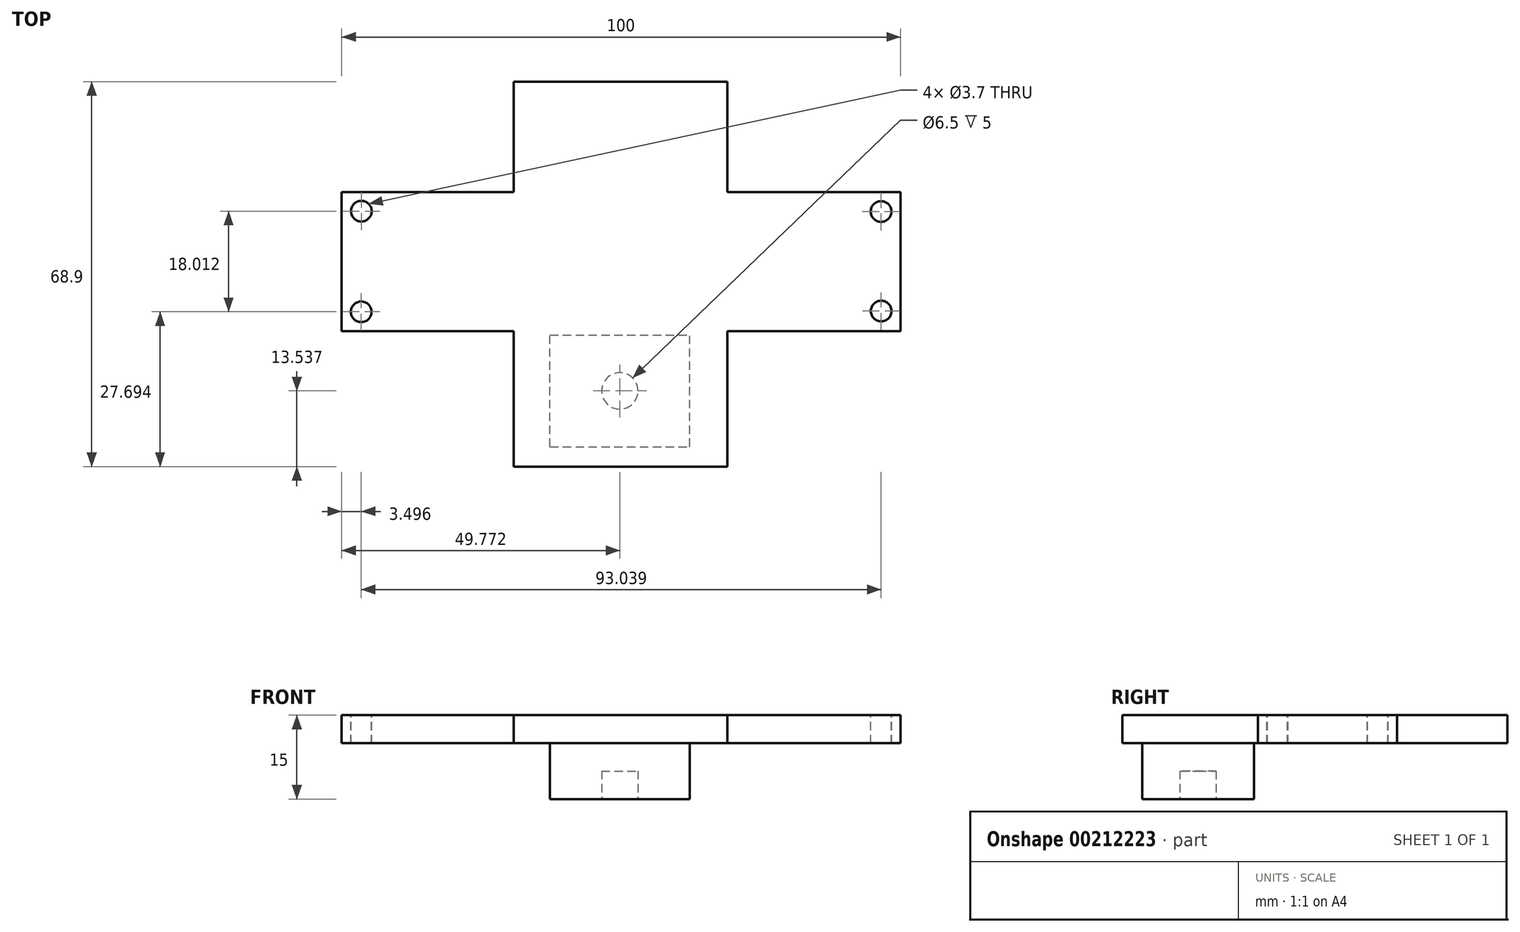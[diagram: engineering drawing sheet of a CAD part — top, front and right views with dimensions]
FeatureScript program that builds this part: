
annotation { "Feature Type Name" : "Feature", "Feature Type Description" : "" }
export const myFeature = defineFeature(function(context is Context, id is Id, definition is map)
    precondition{}
    {
        {
            var Q0;
            Q0=qCreatedBy(makeId("Top.planeOp"),FACE);
            var sketch = newSketch(context, id + "F0", { "sketchPlane" : qUnion([Q0])});
            skLineSegment(sketch, "E0.0", {"start": v(-14.14, 50.77) * mm, "end": v(-14.14, -18.13) * mm});
            skLineSegment(sketch, "E0.1", {"start": v(24.09, 50.77) * mm, "end": v(-14.14, 50.77) * mm});
            skLineSegment(sketch, "E0.2", {"start": v(24.09, -18.13) * mm, "end": v(24.09, 50.77) * mm});
            skLineSegment(sketch, "E0.3", {"start": v(-14.14, -18.13) * mm, "end": v(24.09, -18.13) * mm});
            skSolve(sketch);
        }
        {
            var Q0;
            Q0=makeQuery(id+"F0.imprint","IMPRINT",FACE,{"disambiguationData":[TD([[makeQuery(id+"F0.imprint","IMPRINT",EDGE,{"derivedFrom":sQuery(id+"F0.wireOp",EDGE,"E0.0")}),1.0]])]});
            extrude(context, id + "F1", {"entities" : qUnion([Q0]), "oppositeDirection" : true, "depth" : 5 * mm});
        }
        {
            var Q0;
            {var subQ0=sQuery(id+"F0.wireOp",EDGE,"E0.3");var subQ1=sQuery(id+"F0.wireOp",EDGE,"E0.2");var subQ2=sQuery(id+"F0.wireOp",EDGE,"E0.1");var subQ3=sQuery(id+"F0.wireOp",EDGE,"E0.0");var subQ4=makeQuery(id+"F1.opExtrude","CAP_FACE",FACE,{"disambiguationData":[OSD([subQ3,subQ2,subQ1,subQ0])],"isStart":false});Q0=makeQuery(id+"Fd6R5kjteLHRa52_2.boolean.opBoolean","MERGE",FACE,{"derivedFrom":[makeQuery(id+"FHMCKp7cXqCnkDy_2.boolean.opBoolean","SPLIT",FACE,{"disambiguationData":[TD([makeQuery(id+"F1.opExtrude","SWEPT_FACE",FACE,{"disambiguationData":[OSD([subQ3])]})])],"derivedFrom":subQ4}),makeQuery(id+"FHMCKp7cXqCnkDy_2.boolean.opBoolean","SPLIT",FACE,{"disambiguationData":[TD([makeQuery(id+"FHMCKp7cXqCnkDy_2.opExtrude","SWEPT_FACE",FACE,{"disambiguationData":[OSD([sQuery(id+"FxYa3pFgnVwlmmu_2.wireOp",EDGE,"wV9iuwiv-zcHe-cE0k-HwwL-fQ0fSy19g1jQ")])]})])],"derivedFrom":subQ4}),makeQuery(id+"FHMCKp7cXqCnkDy_2.boolean.opBoolean","SPLIT",FACE,{"disambiguationData":[TD([makeQuery(id+"FHMCKp7cXqCnkDy_2.opExtrude","SWEPT_FACE",FACE,{"disambiguationData":[OSD([sQuery(id+"FxYa3pFgnVwlmmu_2.wireOp",EDGE,"v6R7sFhp-tAEI-SnQt-5ool-xOl96yPjNEbj")])]})])],"derivedFrom":subQ4}),makeQuery(id+"Fd6R5kjteLHRa52_2.opExtrude","CAP_FACE",FACE,{"disambiguationData":[OSD([sQuery(id+"FROp5tmwjT7rY64_2.wireOp",EDGE,"ujx7RY2C-ikGR-Rqo8-pPIV-xWSe6QNDzv8Z.bottom"),sQuery(id+"FROp5tmwjT7rY64_2.wireOp",EDGE,"ujx7RY2C-ikGR-Rqo8-pPIV-xWSe6QNDzv8Z.top"),sQuery(id+"FROp5tmwjT7rY64_2.wireOp",EDGE,"ujx7RY2C-ikGR-Rqo8-pPIV-xWSe6QNDzv8Z.left"),sQuery(id+"FROp5tmwjT7rY64_2.wireOp",EDGE,"ujx7RY2C-ikGR-Rqo8-pPIV-xWSe6QNDzv8Z.right")])],"isStart":true})]});}
            var sketch = newSketch(context, id + "F2", { "sketchPlane" : qUnion([Q0])});
            skLineSegment(sketch, "E1.bottom", {"start": v(-44.9, -31.01) * mm, "end": v(55.1, -31.01) * mm});
            skLineSegment(sketch, "E1.top", {"start": v(-44.9, -6.1) * mm, "end": v(55.1, -6.1) * mm});
            skLineSegment(sketch, "E1.left", {"start": v(-44.9, -31.01) * mm, "end": v(-44.9, -6.1) * mm});
            skLineSegment(sketch, "E1.right", {"start": v(55.1, -31.01) * mm, "end": v(55.1, -6.1) * mm});
            skPoint(sketch, "E2.endSnap0", {"position": v(4.98, -50.77) * mm});
            skSolve(sketch);
        }
        {
            var Q0;
            Q0=qSketchRegion(id+"F2",true);
            extrude(context, id + "F3", {"entities" : qUnion([Q0]), "operationType" : NewBodyOperationType.ADD, "oppositeDirection" : true, "depth" : 5 * mm});
        }
        {
            var Q0;
            Q0=makeQuery(id+"F3.boolean.opBoolean","MERGE",FACE,{"derivedFrom":[makeQuery(id+"F1.opExtrude","CAP_FACE",FACE,{"disambiguationData":[OSD([sQuery(id+"F0.wireOp",EDGE,"E0.0"),sQuery(id+"F0.wireOp",EDGE,"E0.1"),sQuery(id+"F0.wireOp",EDGE,"E0.2"),sQuery(id+"F0.wireOp",EDGE,"E0.3")])],"isStart":true}),makeQuery(id+"F3.opExtrude","CAP_FACE",FACE,{"disambiguationData":[OSD([sQuery(id+"F2.wireOp",EDGE,"E1.bottom"),sQuery(id+"F2.wireOp",EDGE,"E1.top"),sQuery(id+"F2.wireOp",EDGE,"E1.left"),sQuery(id+"F2.wireOp",EDGE,"E1.right")])],"isStart":false})]});
            var sketch = newSketch(context, id + "F4", { "sketchPlane" : qUnion([Q0])});
            skCircle(sketch, "E3", {"center": v(-41.39, 27.58) * mm, "radius": 1.85 * mm});
            skCircle(sketch, "E4", {"center": v(51.6, 27.51) * mm, "radius": 1.85 * mm});
            skLineSegment(sketch, "E5", {"start": v(-44.9, 31.01) * mm, "end": v(-41.4, 31.01) * mm});
            skCircle(sketch, "E6", {"center": v(-41.41, 9.56) * mm, "radius": 1.85 * mm});
            skCircle(sketch, "E7", {"center": v(51.62, 9.7) * mm, "radius": 1.85 * mm});
            skSolve(sketch);
        }
        {
            var Q0;
            Q0=qSketchRegion(id+"F4",true);
            extrude(context, id + "F5", {"entities" : qUnion([Q0]), "operationType" : NewBodyOperationType.REMOVE, "oppositeDirection" : true, "depth" : 25.4 * mm});
        }
        {
            var Q0;
            Q0=makeQuery(id+"F3.boolean.opBoolean","MERGE",FACE,{"derivedFrom":[makeQuery(id+"F1.opExtrude","CAP_FACE",FACE,{"disambiguationData":[OSD([sQuery(id+"F0.wireOp",EDGE,"E0.0"),sQuery(id+"F0.wireOp",EDGE,"E0.1"),sQuery(id+"F0.wireOp",EDGE,"E0.2"),sQuery(id+"F0.wireOp",EDGE,"E0.3")])],"isStart":false}),makeQuery(id+"F3.opExtrude","CAP_FACE",FACE,{"disambiguationData":[OSD([sQuery(id+"F2.wireOp",EDGE,"E1.bottom"),sQuery(id+"F2.wireOp",EDGE,"E1.top"),sQuery(id+"F2.wireOp",EDGE,"E1.left"),sQuery(id+"F2.wireOp",EDGE,"E1.right")])],"isStart":true})]});
            var sketch = newSketch(context, id + "F6", { "sketchPlane" : qUnion([Q0])});
            skLineSegment(sketch, "E8.bottom", {"start": v(-7.64, 14.6) * mm, "end": v(17.36, 14.6) * mm});
            skLineSegment(sketch, "E8.top", {"start": v(-7.64, -5.4) * mm, "end": v(17.36, -5.4) * mm});
            skLineSegment(sketch, "E8.left", {"start": v(-7.64, 14.6) * mm, "end": v(-7.64, -5.4) * mm});
            skLineSegment(sketch, "E8.right", {"start": v(17.36, 14.6) * mm, "end": v(17.36, -5.4) * mm});
            skSolve(sketch);
        }
        {
            var Q0;
            Q0=makeQuery(id+"F6.imprint","IMPRINT",FACE,{"disambiguationData":[TD([[makeQuery(id+"F6.imprint","IMPRINT",EDGE,{"derivedFrom":sQuery(id+"F6.wireOp",EDGE,"E8.bottom")}),-1.0]])]});
            extrude(context, id + "F7", {"entities" : qUnion([Q0]), "operationType" : NewBodyOperationType.ADD, "depth" : 10 * mm});
        }
        {
            var Q0;
            Q0=makeQuery(id+"F7.opExtrude","CAP_FACE",FACE,{"disambiguationData":[OSD([sQuery(id+"F6.wireOp",EDGE,"E8.bottom"),sQuery(id+"F6.wireOp",EDGE,"E8.top"),sQuery(id+"F6.wireOp",EDGE,"E8.left"),sQuery(id+"F6.wireOp",EDGE,"E8.right")])],"isStart":false});
            var sketch = newSketch(context, id + "F8", { "sketchPlane" : qUnion([Q0])});
            skCircle(sketch, "E9", {"center": v(4.86, 4.6) * mm, "radius": 3.25 * mm});
            skSolve(sketch);
        }
        {
            var Q0;
            Q0=makeQuery(id+"F8.imprint","IMPRINT",FACE,{"disambiguationData":[TD([[makeQuery(id+"F8.imprint","IMPRINT",EDGE,{"derivedFrom":sQuery(id+"F8.wireOp",EDGE,"E9")}),1.0]])]});
            extrude(context, id + "F9", {"entities" : qUnion([Q0]), "operationType" : NewBodyOperationType.REMOVE, "oppositeDirection" : true, "depth" : 5 * mm});
        }
    });
